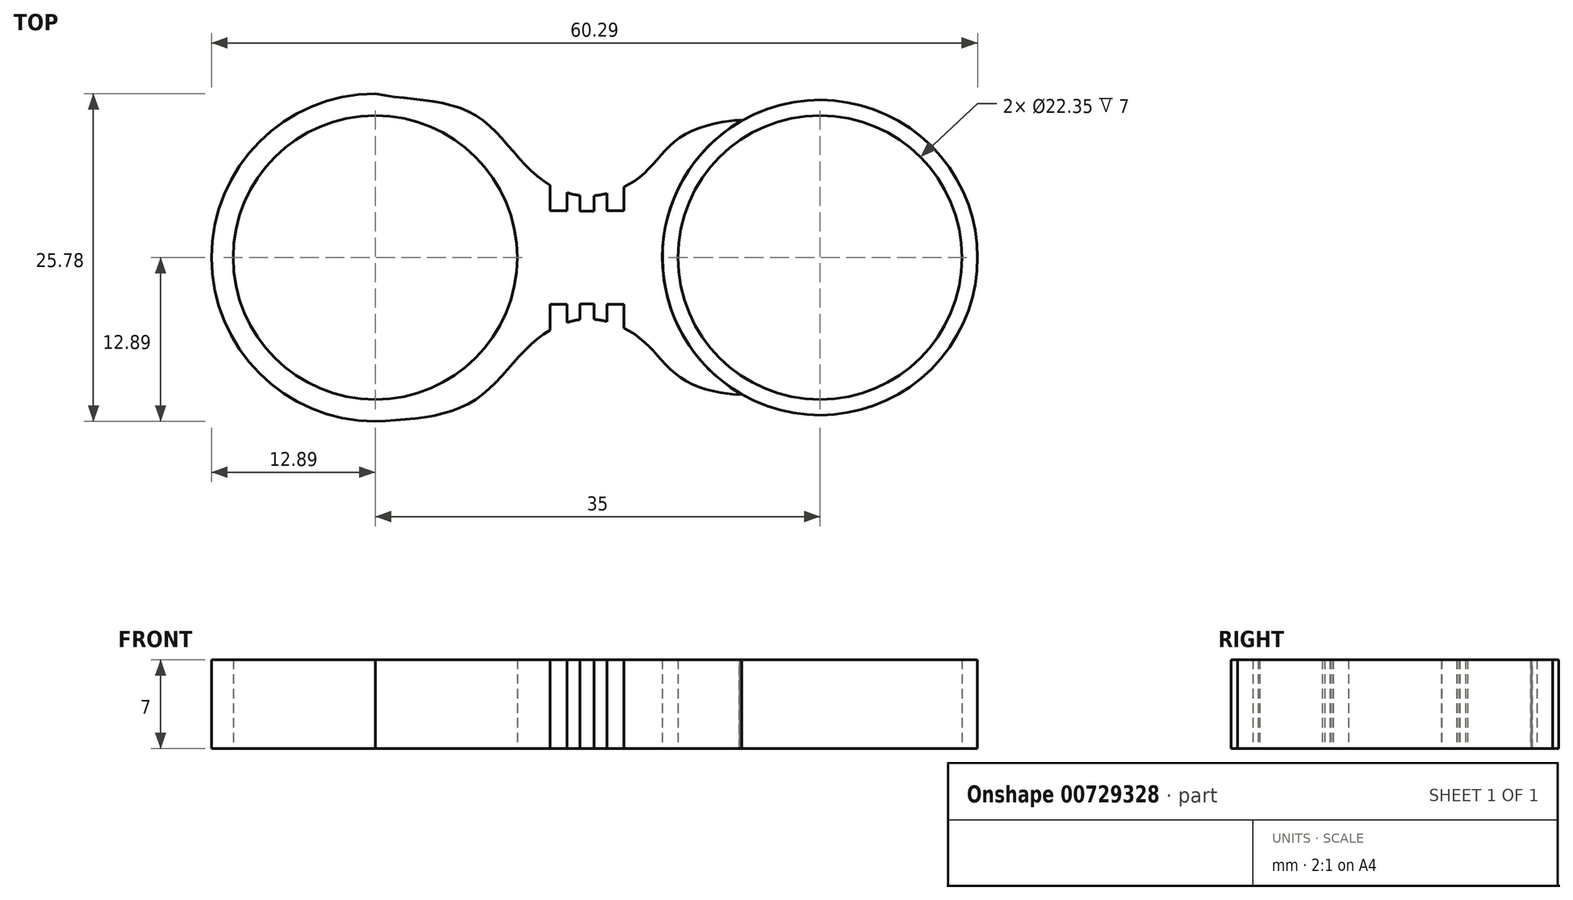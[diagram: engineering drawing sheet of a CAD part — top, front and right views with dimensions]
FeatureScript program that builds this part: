
annotation { "Feature Type Name" : "Feature", "Feature Type Description" : "" }
export const myFeature = defineFeature(function(context is Context, id is Id, definition is map)
    precondition{}
    {
        {
            var Q0;
            Q0=qCreatedBy(makeId("Top.planeOp"),FACE);
            var sketch = newSketch(context, id + "F0", { "sketchPlane" : qUnion([Q0])});
            skCircle(sketch, "E0", {"center": v(0, 0) * mm, "radius": 11.18 * mm});
            skCircle(sketch, "E1", {"center": v(0, 0) * mm, "radius": 12.4 * mm});
            skCircle(sketch, "E2", {"center": v(-35, 0) * mm, "radius": 11.18 * mm});
            skArc(sketch, "E3", {"start": v(-47.89, 0) * mm, "mid": v(-44.11, 9.11) * mm, "end": v(-35, 12.89) * mm});
            skFitSpline(sketch, "E4", {"points": [v(-35, 12.89) * mm, v(-27.43, 11.38) * mm, v(-22.74, 6.83) * mm, v(-18.34, 4.84) * mm, v(-13.93, 6.55) * mm, v(-10.1, 9.96) * mm, v(-6.17, 10.75) * mm, v(-6.34, 10.65) * mm], "startDerivative": vector(39.3, -7.83) * mm, "endDerivative": vector(6.33, -0.1) * mm});
            skArc(sketch, "E5.MirrorCS", {"start": v(-47.89, 0) * mm, "mid": v(-44.11, -9.11) * mm, "end": v(-35, -12.89) * mm});
            skFitSpline(sketch, "E6.MirrorCS", {"points": [v(-35, -12.89) * mm, v(-27.43, -11.38) * mm, v(-22.74, -6.83) * mm, v(-18.34, -4.84) * mm, v(-13.93, -6.55) * mm, v(-10.1, -9.96) * mm, v(-6.17, -10.75) * mm, v(-6.34, -10.65) * mm], "startDerivative": vector(43.01, 2.28) * mm, "endDerivative": vector(-9.05, 3.86) * mm});
            skLineSegment(sketch, "E7.bottom", {"start": v(-21.23, -6.8) * mm, "end": v(-19.92, -6.8) * mm});
            skLineSegment(sketch, "E7.top", {"start": v(-21.23, -3.67) * mm, "end": v(-19.92, -3.67) * mm});
            skLineSegment(sketch, "E7.left", {"start": v(-21.23, -6.8) * mm, "end": v(-21.23, -3.67) * mm});
            skLineSegment(sketch, "E7.right", {"start": v(-19.92, -6.8) * mm, "end": v(-19.92, -3.67) * mm});
            skLineSegment(sketch, "E8.bottom", {"start": v(-17.8, -3.66) * mm, "end": v(-18.88, -3.66) * mm});
            skLineSegment(sketch, "E8.top", {"start": v(-17.8, -6.03) * mm, "end": v(-18.88, -6.03) * mm});
            skLineSegment(sketch, "E8.left", {"start": v(-17.8, -3.66) * mm, "end": v(-17.8, -6.03) * mm});
            skLineSegment(sketch, "E8.right", {"start": v(-18.88, -3.66) * mm, "end": v(-18.88, -6.03) * mm});
            skLineSegment(sketch, "E9.MirrorCS", {"start": v(-15.44, -3.67) * mm, "end": v(-16.76, -3.67) * mm});
            skLineSegment(sketch, "E10.MirrorCS", {"start": v(-16.76, -6.8) * mm, "end": v(-16.76, -3.67) * mm});
            skLineSegment(sketch, "E11.MirrorCS", {"start": v(-15.44, -6.8) * mm, "end": v(-16.76, -6.8) * mm});
            skLineSegment(sketch, "E12.MirrorCS", {"start": v(-15.44, -6.8) * mm, "end": v(-15.44, -3.67) * mm});
            skLineSegment(sketch, "E13.MirrorCS", {"start": v(-21.23, 3.67) * mm, "end": v(-19.92, 3.67) * mm});
            skLineSegment(sketch, "E14.MirrorCS", {"start": v(-17.8, 3.66) * mm, "end": v(-18.88, 3.66) * mm});
            skLineSegment(sketch, "E15.MirrorCS", {"start": v(-17.8, 3.66) * mm, "end": v(-17.8, 6.03) * mm});
            skLineSegment(sketch, "E16.MirrorCS", {"start": v(-15.44, 3.67) * mm, "end": v(-16.76, 3.67) * mm});
            skLineSegment(sketch, "E17.MirrorCS", {"start": v(-15.44, 6.8) * mm, "end": v(-15.44, 3.67) * mm});
            skLineSegment(sketch, "E18.MirrorCS", {"start": v(-15.44, 6.8) * mm, "end": v(-16.76, 6.8) * mm});
            skLineSegment(sketch, "E19.MirrorCS", {"start": v(-16.76, 6.8) * mm, "end": v(-16.76, 3.67) * mm});
            skLineSegment(sketch, "E20.MirrorCS", {"start": v(-17.8, 6.03) * mm, "end": v(-18.88, 6.03) * mm});
            skLineSegment(sketch, "E21.MirrorCS", {"start": v(-18.88, 3.66) * mm, "end": v(-18.88, 6.03) * mm});
            skLineSegment(sketch, "E22.MirrorCS", {"start": v(-19.92, 6.8) * mm, "end": v(-19.92, 3.67) * mm});
            skLineSegment(sketch, "E23.MirrorCS", {"start": v(-21.23, 6.8) * mm, "end": v(-19.92, 6.8) * mm});
            skLineSegment(sketch, "E24.MirrorCS", {"start": v(-21.23, 6.8) * mm, "end": v(-21.23, 3.67) * mm});
            skSolve(sketch);
        }
        {
            var Q0;
            Q0=makeQuery(id+"F0.imprint","IMPRINT",FACE,{"disambiguationData":[TD([[makeQuery(id+"F0.imprint","IMPRINT",EDGE,{"derivedFrom":sQuery(id+"F0.wireOp",EDGE,"E2")}),-1.0]])]});
            extrude(context, id + "F1", {"entities" : qUnion([Q0]), "depth" : 7 * mm, "offsetDistance" : 25.4 * mm});
        }
        {
            var Q0;
            Q0=makeQuery(id+"F0.imprint","IMPRINT",FACE,{"disambiguationData":[TD([[makeQuery(id+"F0.imprint","IMPRINT",EDGE,{"derivedFrom":sQuery(id+"F0.wireOp",EDGE,"E0")}),-1.0]])]});
            extrude(context, id + "F2", {"entities" : qUnion([Q0]), "depth" : 7 * mm, "offsetDistance" : 25.4 * mm});
        }
    });
